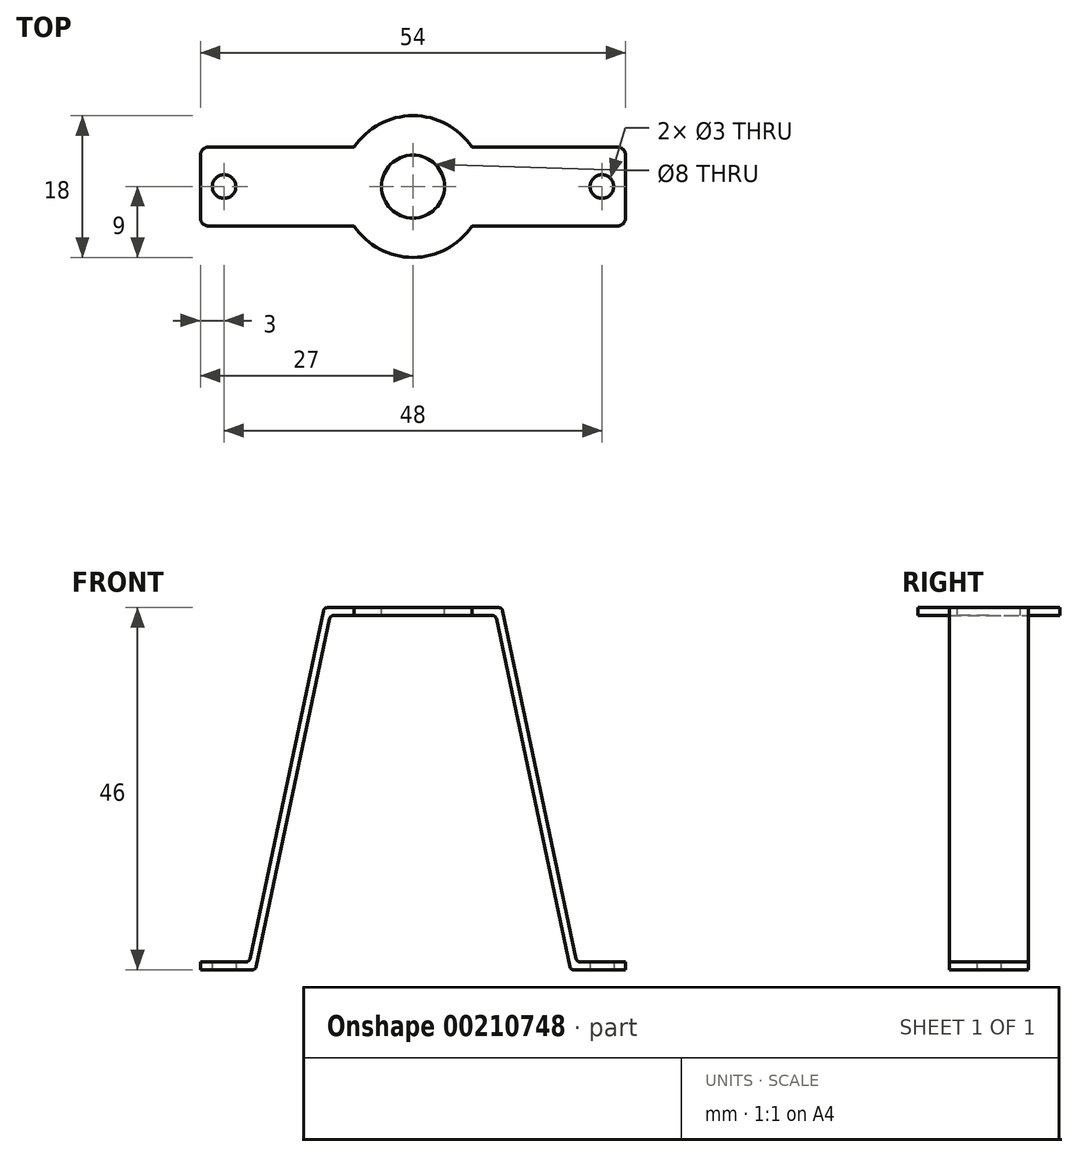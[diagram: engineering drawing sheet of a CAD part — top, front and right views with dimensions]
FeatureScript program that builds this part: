
annotation { "Feature Type Name" : "Feature", "Feature Type Description" : "" }
export const myFeature = defineFeature(function(context is Context, id is Id, definition is map)
    precondition{}
    {
        {
            var Q0;
            Q0=qCreatedBy(makeId("Front.planeOp"),FACE);
            var sketch = newSketch(context, id + "F0", { "sketchPlane" : qUnion([Q0])});
            skLineSegment(sketch, "E0", {"start": v(0, -15.82) * mm, "end": v(0, 53.54) * mm, "construction": true});
            skLineSegment(sketch, "E1", {"start": v(-27, 0) * mm, "end": v(-20, 0) * mm});
            skLineSegment(sketch, "E2", {"start": v(-20, 0) * mm, "end": v(-10.5, 45) * mm});
            skLineSegment(sketch, "E3.MirrorCS", {"start": v(20, 0) * mm, "end": v(10.5, 45) * mm});
            skLineSegment(sketch, "E4.MirrorCS", {"start": v(27, 0) * mm, "end": v(20, 0) * mm});
            skLineSegment(sketch, "E5", {"start": v(-10.5, 45) * mm, "end": v(10.5, 45) * mm});
            skSolve(sketch);
        }
        {
            var Q0;
            Q0=qCreatedBy(makeId("Right.planeOp"),FACE);
            var Q1;
            Q1=sQuery(id+"F0.wireOp",VERTEX,"E4.MirrorCS.start");
            cPlane(context, id + "F1", {"entities" : qUnion([Q0, Q1]), "cplaneType" : CPlaneType.PLANE_POINT, "offset" : 25 * mm, "width" : 150 * mm, "height" : 150 * mm});
        }
        {
            var Q0;
            Q0=qCreatedBy(id+"F1.planeOp",FACE);
            var sketch = newSketch(context, id + "F2", { "sketchPlane" : qUnion([Q0])});
            skLineSegment(sketch, "E6.bottom", {"start": v(-5, 1) * mm, "end": v(5, 1) * mm});
            skLineSegment(sketch, "E6.top", {"start": v(-5, 0) * mm, "end": v(5, 0) * mm});
            skLineSegment(sketch, "E6.left", {"start": v(-5, 1) * mm, "end": v(-5, 0) * mm});
            skLineSegment(sketch, "E6.right", {"start": v(5, 1) * mm, "end": v(5, 0) * mm});
            skSolve(sketch);
        }
        {
            var Q0;
            Q0=makeQuery(id+"F2.imprint","IMPRINT",FACE,{"disambiguationData":[TD([[makeQuery(id+"F2.imprint","IMPRINT",EDGE,{"derivedFrom":sQuery(id+"F2.wireOp",EDGE,"E6.bottom")}),-1.0]])]});
            var Q1;
            Q1=sQuery(id+"F0.wireOp",EDGE,"E4.MirrorCS");
            var Q2;
            Q2=sQuery(id+"F0.wireOp",EDGE,"E3.MirrorCS");
            var Q3;
            Q3=sQuery(id+"F0.wireOp",EDGE,"E5");
            var Q4;
            Q4=sQuery(id+"F0.wireOp",EDGE,"E2");
            var Q5;
            Q5=sQuery(id+"F0.wireOp",EDGE,"E1");
            sweep(context, id + "F3", {"profiles" : qUnion([Q0]), "path" : qUnion([Q1, Q2, Q3, Q4, Q5])});
        }
        {
            var Q0;
            Q0=makeQuery(id+"F3.opSweep","MID_CAP_EDGE",EDGE,{"disambiguationData":[OSD([sQuery(id+"F0.wireOp",VERTEX,"E3.MirrorCS.start"),sQuery(id+"F2.wireOp",EDGE,"E6.bottom")])],"capPos":1.0});
            var Q1;
            Q1=makeQuery(id+"F3.opSweep","MID_CAP_EDGE",EDGE,{"disambiguationData":[OSD([sQuery(id+"F0.wireOp",VERTEX,"E5.end"),sQuery(id+"F2.wireOp",EDGE,"E6.bottom")])],"capPos":2.0});
            var Q2;
            Q2=makeQuery(id+"F3.opSweep","MID_CAP_EDGE",EDGE,{"disambiguationData":[OSD([sQuery(id+"F0.wireOp",VERTEX,"E2.end"),sQuery(id+"F2.wireOp",EDGE,"E6.bottom")])],"capPos":3.0});
            var Q3;
            Q3=makeQuery(id+"F3.opSweep","MID_CAP_EDGE",EDGE,{"disambiguationData":[OSD([sQuery(id+"F0.wireOp",VERTEX,"E1.end"),sQuery(id+"F2.wireOp",EDGE,"E6.bottom")])],"capPos":4.0});
            var Q4;
            Q4=makeQuery(id+"F3.opSweep","MID_CAP_EDGE",EDGE,{"disambiguationData":[OSD([sQuery(id+"F0.wireOp",VERTEX,"E3.MirrorCS.start"),sQuery(id+"F2.wireOp",EDGE,"E6.top")])],"capPos":1.0});
            var Q5;
            Q5=makeQuery(id+"F3.opSweep","MID_CAP_EDGE",EDGE,{"disambiguationData":[OSD([sQuery(id+"F0.wireOp",VERTEX,"E5.end"),sQuery(id+"F2.wireOp",EDGE,"E6.top")])],"capPos":2.0});
            var Q6;
            Q6=makeQuery(id+"F3.opSweep","MID_CAP_EDGE",EDGE,{"disambiguationData":[OSD([sQuery(id+"F0.wireOp",VERTEX,"E1.end"),sQuery(id+"F2.wireOp",EDGE,"E6.top")])],"capPos":4.0});
            var Q7;
            Q7=makeQuery(id+"F3.opSweep","MID_CAP_EDGE",EDGE,{"disambiguationData":[OSD([sQuery(id+"F0.wireOp",VERTEX,"E2.end"),sQuery(id+"F2.wireOp",EDGE,"E6.top")])],"capPos":3.0});
            fillet(context, id + "F4", {"entities" : qUnion([Q0, Q1, Q2, Q3, Q4, Q5, Q6, Q7]), "radius" : 0.5 * mm, "tangentPropagation" : true, "allowEdgeOverflow" : false});
        }
        {
            var Q0;
            Q0=makeQuery(id+"F3.opSweep","SWEPT_FACE",FACE,{"disambiguationData":[OSD([sQuery(id+"F0.wireOp",EDGE,"E5"),sQuery(id+"F2.wireOp",EDGE,"E6.bottom")])]});
            var sketch = newSketch(context, id + "F5", { "sketchPlane" : qUnion([Q0])});
            skCircle(sketch, "E7", {"center": v(0, 0) * mm, "radius": 9 * mm});
            skSolve(sketch);
        }
        {
            var Q0;
            Q0 = qSketchRegion(id + "F5", true);
            var Q1;
            Q1=makeQuery(id+"F3.opSweep","SWEPT_FACE",FACE,{"disambiguationData":[OSD([sQuery(id+"F0.wireOp",EDGE,"E5"),sQuery(id+"F2.wireOp",EDGE,"E6.top")])]});
            extrude(context, id + "F6", {"entities" : qUnion([Q0]), "operationType" : NewBodyOperationType.ADD, "endBound" : BoundingType.UP_TO_SURFACE, "oppositeDirection" : true, "endBoundEntityFace" : qUnion([Q1]), "depth" : 25 * mm});
        }
        {
            var Q0;
            Q0=makeQuery(id+"F6.boolean.opBoolean","MERGE",FACE,{"derivedFrom":[makeQuery(id+"F3.opSweep","SWEPT_FACE",FACE,{"disambiguationData":[OSD([sQuery(id+"F0.wireOp",EDGE,"E5"),sQuery(id+"F2.wireOp",EDGE,"E6.bottom")])]}),makeQuery(id+"F6.opExtrude","CAP_FACE",FACE,{"disambiguationData":[OSD([sQuery(id+"F5.wireOp",EDGE,"E7")])],"isStart":true})]});
            var sketch = newSketch(context, id + "F7", { "sketchPlane" : qUnion([Q0])});
            skCircle(sketch, "E8", {"center": v(0, 0) * mm, "radius": 4 * mm});
            skSolve(sketch);
        }
        {
            var Q0;
            Q0 = qSketchRegion(id + "F7", true);
            extrude(context, id + "F8", {"entities" : qUnion([Q0]), "operationType" : NewBodyOperationType.REMOVE, "endBound" : BoundingType.UP_TO_NEXT, "oppositeDirection" : true, "depth" : 25 * mm});
        }
        {
            var Q0;
            Q0=qCreatedBy(makeId("Top.planeOp"),FACE);
            var sketch = newSketch(context, id + "F9", { "sketchPlane" : qUnion([Q0])});
            skCircle(sketch, "E9", {"center": v(-24, 0) * mm, "radius": 1.5 * mm});
            skCircle(sketch, "E10", {"center": v(24, 0) * mm, "radius": 1.5 * mm});
            skLineSegment(sketch, "E11", {"start": v(-24, 0) * mm, "end": v(24, 0) * mm, "construction": true});
            skSolve(sketch);
        }
        {
            var Q0;
            Q0 = qSketchRegion(id + "F9", true);
            extrude(context, id + "F10", {"entities" : qUnion([Q0]), "operationType" : NewBodyOperationType.REMOVE, "endBound" : BoundingType.UP_TO_NEXT, "depth" : 25 * mm});
        }
        {
            var Q0;
            Q0=makeQuery(id+"F3.opSweep","CAP_EDGE",EDGE,{"disambiguationData":[OSD([sQuery(id+"F0.wireOp",VERTEX,"E4.MirrorCS.start"),sQuery(id+"F2.wireOp",EDGE,"E6.left")])],"isStart":true});
            var Q1;
            Q1=makeQuery(id+"F3.opSweep","CAP_EDGE",EDGE,{"disambiguationData":[OSD([sQuery(id+"F0.wireOp",VERTEX,"E4.MirrorCS.start"),sQuery(id+"F2.wireOp",EDGE,"E6.right")])],"isStart":true});
            var Q2;
            Q2=makeQuery(id+"F3.opSweep","CAP_EDGE",EDGE,{"disambiguationData":[OSD([sQuery(id+"F0.wireOp",VERTEX,"E1.start"),sQuery(id+"F2.wireOp",EDGE,"E6.right")])],"isStart":false});
            var Q3;
            Q3=makeQuery(id+"F3.opSweep","CAP_EDGE",EDGE,{"disambiguationData":[OSD([sQuery(id+"F0.wireOp",VERTEX,"E1.start"),sQuery(id+"F2.wireOp",EDGE,"E6.left")])],"isStart":false});
            fillet(context, id + "F11", {"entities" : qUnion([Q0, Q1, Q2, Q3]), "radius" : 1 * mm, "tangentPropagation" : true, "allowEdgeOverflow" : false});
        }
    });
